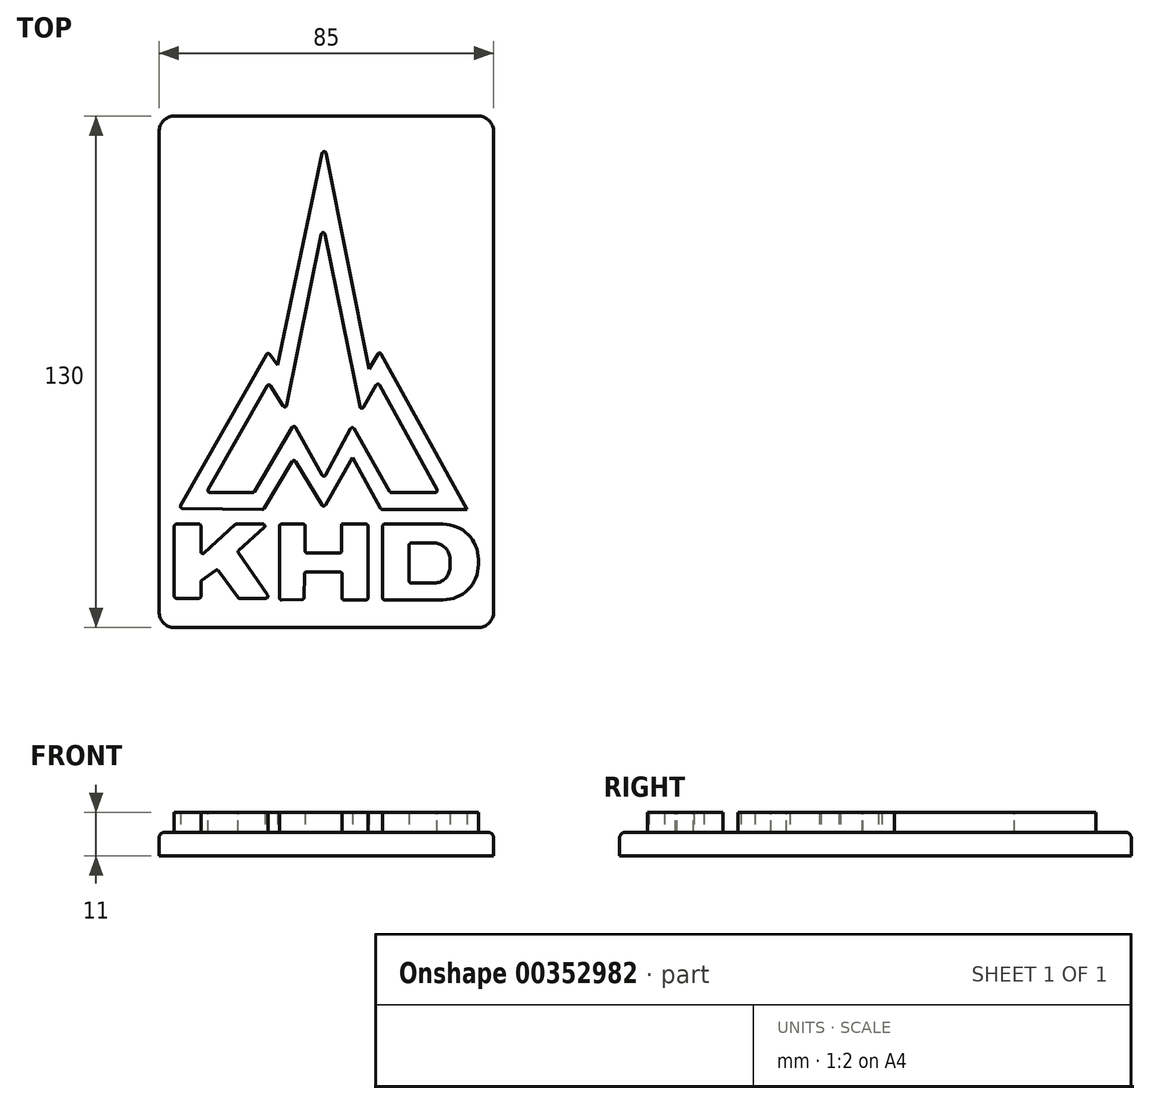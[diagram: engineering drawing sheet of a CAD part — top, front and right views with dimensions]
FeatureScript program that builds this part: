
annotation { "Feature Type Name" : "Feature", "Feature Type Description" : "" }
export const myFeature = defineFeature(function(context is Context, id is Id, definition is map)
    precondition{}
    {
        {
            var Q0;
            Q0=qCreatedBy(makeId("Top.planeOp"),FACE);
            var sketch = newSketch(context, id + "F0", { "sketchPlane" : qUnion([Q0])});
            skLineSegment(sketch, "E0", {"start": v(-38.63, -38.72) * mm, "end": v(-31.87, -38.72) * mm});
            skLineSegment(sketch, "E1", {"start": v(-31.87, -38.72) * mm, "end": v(-31.87, -46.83) * mm});
            skLineSegment(sketch, "E2", {"start": v(-31.87, -46.83) * mm, "end": v(-23.05, -38.72) * mm});
            skLineSegment(sketch, "E3", {"start": v(-23.05, -38.72) * mm, "end": v(-14.82, -38.72) * mm});
            skLineSegment(sketch, "E4", {"start": v(-14.82, -38.72) * mm, "end": v(-22.58, -45.66) * mm});
            skLineSegment(sketch, "E5", {"start": v(-22.58, -45.66) * mm, "end": v(-14.4, -57.53) * mm});
            skLineSegment(sketch, "E6", {"start": v(-14.4, -57.53) * mm, "end": v(-22.34, -57.53) * mm});
            skLineSegment(sketch, "E7", {"start": v(-22.34, -57.53) * mm, "end": v(-27.7, -50.18) * mm});
            skLineSegment(sketch, "E8", {"start": v(-27.7, -50.18) * mm, "end": v(-31.87, -53.18) * mm});
            skLineSegment(sketch, "E9", {"start": v(-31.87, -53.18) * mm, "end": v(-31.87, -57.53) * mm});
            skLineSegment(sketch, "E10", {"start": v(-31.87, -57.53) * mm, "end": v(-38.63, -57.53) * mm});
            skLineSegment(sketch, "E11", {"start": v(-38.63, -57.53) * mm, "end": v(-38.63, -38.72) * mm});
            skLineSegment(sketch, "E12", {"start": v(-11.94, -38.72) * mm, "end": v(-5.35, -38.72) * mm});
            skLineSegment(sketch, "E13", {"start": v(-5.35, -38.72) * mm, "end": v(-5.35, -46.07) * mm});
            skLineSegment(sketch, "E14", {"start": v(-5.35, -46.07) * mm, "end": v(3.88, -46.07) * mm});
            skLineSegment(sketch, "E15", {"start": v(3.88, -46.07) * mm, "end": v(3.88, -38.72) * mm});
            skLineSegment(sketch, "E16", {"start": v(3.88, -38.72) * mm, "end": v(10.58, -38.72) * mm});
            skLineSegment(sketch, "E17", {"start": v(10.58, -38.72) * mm, "end": v(10.58, -57.94) * mm});
            skLineSegment(sketch, "E18", {"start": v(10.58, -57.94) * mm, "end": v(3.94, -57.94) * mm});
            skLineSegment(sketch, "E19", {"start": v(3.94, -57.94) * mm, "end": v(4.03, -50.92) * mm});
            skLineSegment(sketch, "E20", {"start": v(4.03, -50.92) * mm, "end": v(-5.53, -50.83) * mm});
            skLineSegment(sketch, "E21", {"start": v(-5.53, -50.83) * mm, "end": v(-5.7, -57.89) * mm});
            skLineSegment(sketch, "E22", {"start": v(-5.7, -57.89) * mm, "end": v(-11.94, -57.94) * mm});
            skLineSegment(sketch, "E23", {"start": v(-11.94, -57.94) * mm, "end": v(-11.94, -38.72) * mm});
            skLineSegment(sketch, "E24", {"start": v(-37.4, -34.66) * mm, "end": v(-15.93, -34.95) * mm});
            skLineSegment(sketch, "E25", {"start": v(-15.93, -34.95) * mm, "end": v(-8.23, -22.08) * mm});
            skLineSegment(sketch, "E26", {"start": v(-8.23, -22.08) * mm, "end": v(-0.68, -34.6) * mm});
            skLineSegment(sketch, "E27", {"start": v(-0.68, -34.6) * mm, "end": v(6.7, -21.78) * mm});
            skLineSegment(sketch, "E28", {"start": v(6.7, -21.78) * mm, "end": v(13.93, -34.95) * mm});
            skLineSegment(sketch, "E29", {"start": v(13.93, -34.95) * mm, "end": v(35.75, -34.95) * mm});
            skLineSegment(sketch, "E30", {"start": v(35.75, -34.95) * mm, "end": v(13.52, 5.32) * mm});
            skLineSegment(sketch, "E31", {"start": v(13.52, 5.32) * mm, "end": v(10.82, 0.7) * mm});
            skLineSegment(sketch, "E32", {"start": v(10.82, 0.7) * mm, "end": v(-0.53, 57.94) * mm});
            skLineSegment(sketch, "E33", {"start": v(-0.53, 57.94) * mm, "end": v(-12.35, 1.7) * mm});
            skLineSegment(sketch, "E34", {"start": v(-12.35, 1.7) * mm, "end": v(-14.88, 5.09) * mm});
            skLineSegment(sketch, "E35", {"start": v(-14.88, 5.09) * mm, "end": v(-37.4, -34.66) * mm});
            skLineSegment(sketch, "E36", {"start": v(38.63, -57.94) * mm, "end": v(14.29, -57.94) * mm});
            skLineSegment(sketch, "E37", {"start": v(14.29, -57.94) * mm, "end": v(14.29, -38.72) * mm});
            skLineSegment(sketch, "E38", {"start": v(14.29, -38.72) * mm, "end": v(38.63, -38.72) * mm});
            skLineSegment(sketch, "E39", {"start": v(38.63, -38.72) * mm, "end": v(38.63, -57.94) * mm});
            skLineSegment(sketch, "E40", {"start": v(31.4, -53.65) * mm, "end": v(21.05, -53.65) * mm});
            skLineSegment(sketch, "E41", {"start": v(21.05, -53.65) * mm, "end": v(21.05, -43.54) * mm});
            skLineSegment(sketch, "E42", {"start": v(21.05, -43.54) * mm, "end": v(31.4, -43.54) * mm});
            skLineSegment(sketch, "E43", {"start": v(31.4, -43.54) * mm, "end": v(31.4, -53.65) * mm});
            skLineSegment(sketch, "E44", {"start": v(-30.46, -30.66) * mm, "end": v(-18.4, -30.66) * mm});
            skLineSegment(sketch, "E45", {"start": v(-18.4, -30.66) * mm, "end": v(-8.23, -13.38) * mm});
            skLineSegment(sketch, "E46", {"start": v(-8.23, -13.38) * mm, "end": v(-0.59, -27.07) * mm});
            skLineSegment(sketch, "E47", {"start": v(-0.59, -27.07) * mm, "end": v(6.59, -13.67) * mm});
            skLineSegment(sketch, "E48", {"start": v(6.59, -13.67) * mm, "end": v(16.23, -30.66) * mm});
            skLineSegment(sketch, "E49", {"start": v(16.23, -30.66) * mm, "end": v(28.52, -30.66) * mm});
            skLineSegment(sketch, "E50", {"start": v(28.52, -30.66) * mm, "end": v(13.11, -2.62) * mm});
            skLineSegment(sketch, "E51", {"start": v(13.11, -2.62) * mm, "end": v(8.76, -10.14) * mm});
            skLineSegment(sketch, "E52", {"start": v(8.76, -10.14) * mm, "end": v(-0.82, 37.37) * mm});
            skLineSegment(sketch, "E53", {"start": v(-0.82, 37.37) * mm, "end": v(-10.29, -9.73) * mm});
            skLineSegment(sketch, "E54", {"start": v(-10.29, -9.73) * mm, "end": v(-14.64, -2.85) * mm});
            skLineSegment(sketch, "E55", {"start": v(-14.64, -2.85) * mm, "end": v(-30.46, -30.66) * mm});
            skSolve(sketch);
        }
        {
            var Q0;
            Q0 = qSketchRegion(id + "F0", true);
            extrude(context, id + "F1", {"entities" : qUnion([Q0]), "depth" : 5 * mm});
        }
        {
            var Q0;
            Q0=makeQuery(id+"F1.opExtrude","SWEPT_EDGE",EDGE,{"disambiguationData":[OSD([sQuery(id+"F0.wireOp",EDGE,"E42"),sQuery(id+"F0.wireOp",EDGE,"E43")])]});
            var Q1;
            Q1=makeQuery(id+"F1.opExtrude","SWEPT_EDGE",EDGE,{"disambiguationData":[OSD([sQuery(id+"F0.wireOp",EDGE,"E40"),sQuery(id+"F0.wireOp",EDGE,"E43")])]});
            fillet(context, id + "F2", {"entities" : qUnion([Q0, Q1]), "radius" : 4 * mm, "tangentPropagation" : true, "allowEdgeOverflow" : false});
        }
        {
            var Q0;
            Q0=makeQuery(id+"F1.opExtrude","SWEPT_EDGE",EDGE,{"disambiguationData":[OSD([sQuery(id+"F0.wireOp",EDGE,"E36"),sQuery(id+"F0.wireOp",EDGE,"E39")])]});
            var Q1;
            Q1=makeQuery(id+"F1.opExtrude","SWEPT_EDGE",EDGE,{"disambiguationData":[OSD([sQuery(id+"F0.wireOp",EDGE,"E38"),sQuery(id+"F0.wireOp",EDGE,"E39")])]});
            fillet(context, id + "F3", {"entities" : qUnion([Q0, Q1]), "radius" : 9 * mm, "tangentPropagation" : true, "allowEdgeOverflow" : false});
        }
        {
            var Q0;
            Q0=makeQuery(id+"F1.opExtrude","SWEPT_EDGE",EDGE,{"disambiguationData":[OSD([sQuery(id+"F0.wireOp",EDGE,"E0"),sQuery(id+"F0.wireOp",EDGE,"E11")])]});
            var Q1;
            Q1=makeQuery(id+"F1.opExtrude","SWEPT_EDGE",EDGE,{"disambiguationData":[OSD([sQuery(id+"F0.wireOp",EDGE,"E0"),sQuery(id+"F0.wireOp",EDGE,"E1")])]});
            var Q2;
            Q2=makeQuery(id+"F1.opExtrude","SWEPT_EDGE",EDGE,{"disambiguationData":[OSD([sQuery(id+"F0.wireOp",EDGE,"E2"),sQuery(id+"F0.wireOp",EDGE,"E3")])]});
            var Q3;
            Q3=makeQuery(id+"F1.opExtrude","SWEPT_EDGE",EDGE,{"disambiguationData":[OSD([sQuery(id+"F0.wireOp",EDGE,"E3"),sQuery(id+"F0.wireOp",EDGE,"E4")])]});
            var Q4;
            Q4=makeQuery(id+"F1.opExtrude","SWEPT_EDGE",EDGE,{"disambiguationData":[OSD([sQuery(id+"F0.wireOp",EDGE,"E1"),sQuery(id+"F0.wireOp",EDGE,"E2")])]});
            var Q5;
            Q5=makeQuery(id+"F1.opExtrude","SWEPT_EDGE",EDGE,{"disambiguationData":[OSD([sQuery(id+"F0.wireOp",EDGE,"E4"),sQuery(id+"F0.wireOp",EDGE,"E5")])]});
            var Q6;
            Q6=makeQuery(id+"F1.opExtrude","SWEPT_EDGE",EDGE,{"disambiguationData":[OSD([sQuery(id+"F0.wireOp",EDGE,"E5"),sQuery(id+"F0.wireOp",EDGE,"E6")])]});
            var Q7;
            Q7=makeQuery(id+"F1.opExtrude","SWEPT_EDGE",EDGE,{"disambiguationData":[OSD([sQuery(id+"F0.wireOp",EDGE,"E6"),sQuery(id+"F0.wireOp",EDGE,"E7")])]});
            var Q8;
            Q8=makeQuery(id+"F1.opExtrude","SWEPT_EDGE",EDGE,{"disambiguationData":[OSD([sQuery(id+"F0.wireOp",EDGE,"E7"),sQuery(id+"F0.wireOp",EDGE,"E8")])]});
            var Q9;
            Q9=makeQuery(id+"F1.opExtrude","SWEPT_EDGE",EDGE,{"disambiguationData":[OSD([sQuery(id+"F0.wireOp",EDGE,"E8"),sQuery(id+"F0.wireOp",EDGE,"E9")])]});
            var Q10;
            Q10=makeQuery(id+"F1.opExtrude","SWEPT_EDGE",EDGE,{"disambiguationData":[OSD([sQuery(id+"F0.wireOp",EDGE,"E9"),sQuery(id+"F0.wireOp",EDGE,"E10")])]});
            var Q11;
            Q11=makeQuery(id+"F1.opExtrude","SWEPT_EDGE",EDGE,{"disambiguationData":[OSD([sQuery(id+"F0.wireOp",EDGE,"E10"),sQuery(id+"F0.wireOp",EDGE,"E11")])]});
            var Q12;
            Q12=makeQuery(id+"F1.opExtrude","SWEPT_EDGE",EDGE,{"disambiguationData":[OSD([sQuery(id+"F0.wireOp",EDGE,"E22"),sQuery(id+"F0.wireOp",EDGE,"E23")])]});
            var Q13;
            Q13=makeQuery(id+"F1.opExtrude","SWEPT_EDGE",EDGE,{"disambiguationData":[OSD([sQuery(id+"F0.wireOp",EDGE,"E21"),sQuery(id+"F0.wireOp",EDGE,"E22")])]});
            var Q14;
            Q14=makeQuery(id+"F1.opExtrude","SWEPT_EDGE",EDGE,{"disambiguationData":[OSD([sQuery(id+"F0.wireOp",EDGE,"E19"),sQuery(id+"F0.wireOp",EDGE,"E20")])]});
            var Q15;
            Q15=makeQuery(id+"F1.opExtrude","SWEPT_EDGE",EDGE,{"disambiguationData":[OSD([sQuery(id+"F0.wireOp",EDGE,"E18"),sQuery(id+"F0.wireOp",EDGE,"E19")])]});
            var Q16;
            Q16=makeQuery(id+"F1.opExtrude","SWEPT_EDGE",EDGE,{"disambiguationData":[OSD([sQuery(id+"F0.wireOp",EDGE,"E17"),sQuery(id+"F0.wireOp",EDGE,"E18")])]});
            var Q17;
            Q17=makeQuery(id+"F1.opExtrude","SWEPT_EDGE",EDGE,{"disambiguationData":[OSD([sQuery(id+"F0.wireOp",EDGE,"E36"),sQuery(id+"F0.wireOp",EDGE,"E37")])]});
            var Q18;
            Q18=makeQuery(id+"F1.opExtrude","SWEPT_EDGE",EDGE,{"disambiguationData":[OSD([sQuery(id+"F0.wireOp",EDGE,"E37"),sQuery(id+"F0.wireOp",EDGE,"E38")])]});
            var Q19;
            Q19=makeQuery(id+"F1.opExtrude","SWEPT_EDGE",EDGE,{"disambiguationData":[OSD([sQuery(id+"F0.wireOp",EDGE,"E28"),sQuery(id+"F0.wireOp",EDGE,"E29")])]});
            var Q20;
            Q20=makeQuery(id+"F1.opExtrude","SWEPT_EDGE",EDGE,{"disambiguationData":[OSD([sQuery(id+"F0.wireOp",EDGE,"E26"),sQuery(id+"F0.wireOp",EDGE,"E27")])]});
            var Q21;
            Q21=makeQuery(id+"F1.opExtrude","SWEPT_EDGE",EDGE,{"disambiguationData":[OSD([sQuery(id+"F0.wireOp",EDGE,"E24"),sQuery(id+"F0.wireOp",EDGE,"E35")])]});
            var Q22;
            Q22=makeQuery(id+"F1.opExtrude","SWEPT_EDGE",EDGE,{"disambiguationData":[OSD([sQuery(id+"F0.wireOp",EDGE,"E24"),sQuery(id+"F0.wireOp",EDGE,"E25")])]});
            var Q23;
            Q23=makeQuery(id+"F1.opExtrude","SWEPT_EDGE",EDGE,{"disambiguationData":[OSD([sQuery(id+"F0.wireOp",EDGE,"E25"),sQuery(id+"F0.wireOp",EDGE,"E26")])]});
            var Q24;
            Q24=makeQuery(id+"F1.opExtrude","SWEPT_EDGE",EDGE,{"disambiguationData":[OSD([sQuery(id+"F0.wireOp",EDGE,"E20"),sQuery(id+"F0.wireOp",EDGE,"E21")])]});
            var Q25;
            Q25=makeQuery(id+"F1.opExtrude","SWEPT_EDGE",EDGE,{"disambiguationData":[OSD([sQuery(id+"F0.wireOp",EDGE,"E40"),sQuery(id+"F0.wireOp",EDGE,"E41")])]});
            var Q26;
            Q26=makeQuery(id+"F1.opExtrude","SWEPT_EDGE",EDGE,{"disambiguationData":[OSD([sQuery(id+"F0.wireOp",EDGE,"E41"),sQuery(id+"F0.wireOp",EDGE,"E42")])]});
            var Q27;
            Q27=makeQuery(id+"F1.opExtrude","SWEPT_EDGE",EDGE,{"disambiguationData":[OSD([sQuery(id+"F0.wireOp",EDGE,"E16"),sQuery(id+"F0.wireOp",EDGE,"E17")])]});
            var Q28;
            Q28=makeQuery(id+"F1.opExtrude","SWEPT_EDGE",EDGE,{"disambiguationData":[OSD([sQuery(id+"F0.wireOp",EDGE,"E12"),sQuery(id+"F0.wireOp",EDGE,"E13")])]});
            var Q29;
            Q29=makeQuery(id+"F1.opExtrude","SWEPT_EDGE",EDGE,{"disambiguationData":[OSD([sQuery(id+"F0.wireOp",EDGE,"E13"),sQuery(id+"F0.wireOp",EDGE,"E14")])]});
            var Q30;
            Q30=makeQuery(id+"F1.opExtrude","SWEPT_EDGE",EDGE,{"disambiguationData":[OSD([sQuery(id+"F0.wireOp",EDGE,"E12"),sQuery(id+"F0.wireOp",EDGE,"E23")])]});
            var Q31;
            Q31=makeQuery(id+"F1.opExtrude","SWEPT_EDGE",EDGE,{"disambiguationData":[OSD([sQuery(id+"F0.wireOp",EDGE,"E14"),sQuery(id+"F0.wireOp",EDGE,"E15")])]});
            var Q32;
            Q32=makeQuery(id+"F1.opExtrude","SWEPT_EDGE",EDGE,{"disambiguationData":[OSD([sQuery(id+"F0.wireOp",EDGE,"E46"),sQuery(id+"F0.wireOp",EDGE,"E47")])]});
            var Q33;
            Q33=makeQuery(id+"F1.opExtrude","SWEPT_EDGE",EDGE,{"disambiguationData":[OSD([sQuery(id+"F0.wireOp",EDGE,"E47"),sQuery(id+"F0.wireOp",EDGE,"E48")])]});
            var Q34;
            Q34=makeQuery(id+"F1.opExtrude","SWEPT_EDGE",EDGE,{"disambiguationData":[OSD([sQuery(id+"F0.wireOp",EDGE,"E48"),sQuery(id+"F0.wireOp",EDGE,"E49")])]});
            var Q35;
            Q35=makeQuery(id+"F1.opExtrude","SWEPT_EDGE",EDGE,{"disambiguationData":[OSD([sQuery(id+"F0.wireOp",EDGE,"E45"),sQuery(id+"F0.wireOp",EDGE,"E46")])]});
            var Q36;
            Q36=makeQuery(id+"F1.opExtrude","SWEPT_EDGE",EDGE,{"disambiguationData":[OSD([sQuery(id+"F0.wireOp",EDGE,"E44"),sQuery(id+"F0.wireOp",EDGE,"E45")])]});
            var Q37;
            Q37=makeQuery(id+"F1.opExtrude","SWEPT_EDGE",EDGE,{"disambiguationData":[OSD([sQuery(id+"F0.wireOp",EDGE,"E44"),sQuery(id+"F0.wireOp",EDGE,"E55")])]});
            var Q38;
            Q38=makeQuery(id+"F1.opExtrude","SWEPT_EDGE",EDGE,{"disambiguationData":[OSD([sQuery(id+"F0.wireOp",EDGE,"E34"),sQuery(id+"F0.wireOp",EDGE,"E35")])]});
            var Q39;
            Q39=makeQuery(id+"F1.opExtrude","SWEPT_EDGE",EDGE,{"disambiguationData":[OSD([sQuery(id+"F0.wireOp",EDGE,"E53"),sQuery(id+"F0.wireOp",EDGE,"E54")])]});
            var Q40;
            Q40=makeQuery(id+"F1.opExtrude","SWEPT_EDGE",EDGE,{"disambiguationData":[OSD([sQuery(id+"F0.wireOp",EDGE,"E51"),sQuery(id+"F0.wireOp",EDGE,"E52")])]});
            var Q41;
            Q41=makeQuery(id+"F1.opExtrude","SWEPT_EDGE",EDGE,{"disambiguationData":[OSD([sQuery(id+"F0.wireOp",EDGE,"E49"),sQuery(id+"F0.wireOp",EDGE,"E50")])]});
            var Q42;
            Q42=makeQuery(id+"F1.opExtrude","SWEPT_EDGE",EDGE,{"disambiguationData":[OSD([sQuery(id+"F0.wireOp",EDGE,"E50"),sQuery(id+"F0.wireOp",EDGE,"E51")])]});
            var Q43;
            Q43=makeQuery(id+"F1.opExtrude","SWEPT_EDGE",EDGE,{"disambiguationData":[OSD([sQuery(id+"F0.wireOp",EDGE,"E30"),sQuery(id+"F0.wireOp",EDGE,"E31")])]});
            var Q44;
            Q44=makeQuery(id+"F1.opExtrude","SWEPT_EDGE",EDGE,{"disambiguationData":[OSD([sQuery(id+"F0.wireOp",EDGE,"E52"),sQuery(id+"F0.wireOp",EDGE,"E53")])]});
            var Q45;
            Q45=makeQuery(id+"F1.opExtrude","SWEPT_EDGE",EDGE,{"disambiguationData":[OSD([sQuery(id+"F0.wireOp",EDGE,"E32"),sQuery(id+"F0.wireOp",EDGE,"E33")])]});
            var Q46;
            Q46=makeQuery(id+"F1.opExtrude","SWEPT_EDGE",EDGE,{"disambiguationData":[OSD([sQuery(id+"F0.wireOp",EDGE,"E54"),sQuery(id+"F0.wireOp",EDGE,"E55")])]});
            fillet(context, id + "F4", {"entities" : qUnion([Q0, Q1, Q2, Q3, Q4, Q5, Q6, Q7, Q8, Q9, Q10, Q11, Q12, Q13, Q14, Q15, Q16, Q17, Q18, Q19, Q20, Q21, Q22, Q23, Q24, Q25, Q26, Q27, Q28, Q29, Q30, Q31, Q32, Q33, Q34, Q35, Q36, Q37, Q38, Q39, Q40, Q41, Q42, Q43, Q44, Q45, Q46]), "radius" : 0.5 * mm, "tangentPropagation" : true, "allowEdgeOverflow" : false});
        }
        {
            var Q0;
            Q0=makeQuery(id+"F1.opExtrude","CAP_FACE",FACE,{"disambiguationData":[OSD([sQuery(id+"F0.wireOp",EDGE,"E0"),sQuery(id+"F0.wireOp",EDGE,"E1"),sQuery(id+"F0.wireOp",EDGE,"E2"),sQuery(id+"F0.wireOp",EDGE,"E3"),sQuery(id+"F0.wireOp",EDGE,"E4"),sQuery(id+"F0.wireOp",EDGE,"E5"),sQuery(id+"F0.wireOp",EDGE,"E6"),sQuery(id+"F0.wireOp",EDGE,"E7"),sQuery(id+"F0.wireOp",EDGE,"E8"),sQuery(id+"F0.wireOp",EDGE,"E9"),sQuery(id+"F0.wireOp",EDGE,"E10"),sQuery(id+"F0.wireOp",EDGE,"E11")])],"isStart":true});
            var sketch = newSketch(context, id + "F5", { "sketchPlane" : qUnion([Q0])});
            skLineSegment(sketch, "E56.bottom", {"start": v(-42.5, 65) * mm, "end": v(42.5, 65) * mm});
            skLineSegment(sketch, "E56.top", {"start": v(-42.5, -65) * mm, "end": v(42.5, -65) * mm});
            skLineSegment(sketch, "E56.left", {"start": v(-42.5, 65) * mm, "end": v(-42.5, -65) * mm});
            skLineSegment(sketch, "E56.right", {"start": v(42.5, 65) * mm, "end": v(42.5, -65) * mm});
            skPoint(sketch, "E56.middle", {"position": v(0, 0) * mm});
            skSolve(sketch);
        }
        {
            var Q0;
            Q0 = qSketchRegion(id + "F5", true);
            extrude(context, id + "F6", {"entities" : qUnion([Q0]), "operationType" : NewBodyOperationType.ADD, "depth" : 6 * mm});
        }
        {
            var Q0;
            Q0=makeQuery(id+"F6.opExtrude","SWEPT_EDGE",EDGE,{"disambiguationData":[OSD([sQuery(id+"F5.wireOp",EDGE,"E56.bottom"),sQuery(id+"F5.wireOp",EDGE,"E56.right")])]});
            var Q1;
            Q1=makeQuery(id+"F6.opExtrude","SWEPT_EDGE",EDGE,{"disambiguationData":[OSD([sQuery(id+"F5.wireOp",EDGE,"E56.top"),sQuery(id+"F5.wireOp",EDGE,"E56.right")])]});
            var Q2;
            Q2=makeQuery(id+"F6.opExtrude","SWEPT_EDGE",EDGE,{"disambiguationData":[OSD([sQuery(id+"F5.wireOp",EDGE,"E56.top"),sQuery(id+"F5.wireOp",EDGE,"E56.left")])]});
            var Q3;
            Q3=makeQuery(id+"F6.opExtrude","SWEPT_EDGE",EDGE,{"disambiguationData":[OSD([sQuery(id+"F5.wireOp",EDGE,"E56.bottom"),sQuery(id+"F5.wireOp",EDGE,"E56.left")])]});
            fillet(context, id + "F7", {"entities" : qUnion([Q0, Q1, Q2, Q3]), "radius" : 4 * mm, "tangentPropagation" : true, "allowEdgeOverflow" : false});
        }
        {
            var Q0;
            Q0=makeQuery(id+"F6.opExtrude","CAP_EDGE",EDGE,{"disambiguationData":[OSD([sQuery(id+"F5.wireOp",EDGE,"E56.bottom")])],"isStart":true});
            fillet(context, id + "F8", {"entities" : qUnion([Q0]), "radius" : 1.5 * mm, "tangentPropagation" : true, "allowEdgeOverflow" : false});
        }
    });
